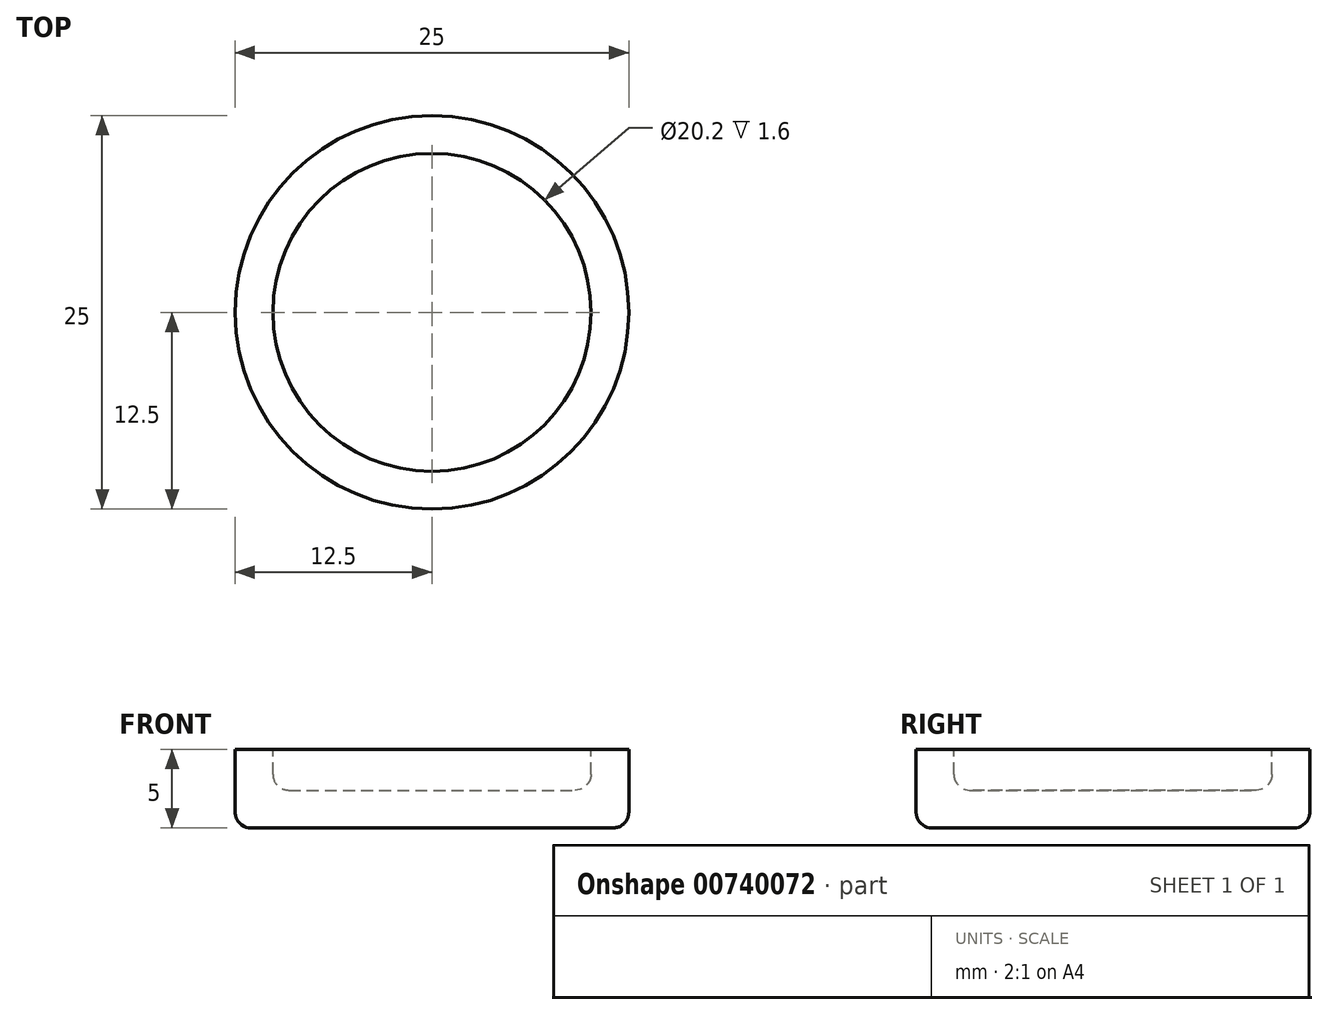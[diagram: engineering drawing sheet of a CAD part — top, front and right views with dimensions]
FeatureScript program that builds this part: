
annotation { "Feature Type Name" : "Feature", "Feature Type Description" : "" }
export const myFeature = defineFeature(function(context is Context, id is Id, definition is map)
    precondition{}
    {
        {
            var Q0;
            Q0=qCreatedBy(makeId("Front.planeOp"),FACE);
            var sketch = newSketch(context, id + "F0", { "sketchPlane" : qUnion([Q0])});
            skLineSegment(sketch, "E0", {"start": v(0, 0) * mm, "end": v(12.5, 0) * mm});
            skLineSegment(sketch, "E1", {"start": v(12.5, 0) * mm, "end": v(12.5, 5) * mm});
            skLineSegment(sketch, "E2", {"start": v(12.5, 5) * mm, "end": v(10.1, 5) * mm});
            skLineSegment(sketch, "E3", {"start": v(10.1, 5) * mm, "end": v(10.1, 2.4) * mm});
            skLineSegment(sketch, "E4", {"start": v(10.1, 2.4) * mm, "end": v(0, 2.4) * mm});
            skLineSegment(sketch, "E5", {"start": v(0, 2.4) * mm, "end": v(0, 0) * mm});
            skSolve(sketch);
        }
        {
            var Q0;
            Q0=makeQuery(id+"F0.imprint","IMPRINT",FACE,{"disambiguationData":[TD([[makeQuery(id+"F0.imprint","IMPRINT",EDGE,{"derivedFrom":sQuery(id+"F0.wireOp",EDGE,"E0")}),1.0]])]});
            var Q1;
            Q1=sQuery(id+"F0.wireOp",EDGE,"E5");
            revolve(context, id + "F1", {"surfaceOperationType" : NewSurfaceOperationType.NEW, "entities" : qUnion([Q0]), "axis" : qUnion([Q1]), "revolveType" : RevolveType.FULL});
        }
        {
            var Q0;
            Q0=makeQuery(id+"F1.opRevolve","SWEPT_EDGE",EDGE,{"disambiguationData":[OSD([sQuery(id+"F0.wireOp",EDGE,"E3"),sQuery(id+"F0.wireOp",EDGE,"E4")])]});
            var Q1;
            Q1=makeQuery(id+"F1.opRevolve","SWEPT_EDGE",EDGE,{"disambiguationData":[OSD([sQuery(id+"F0.wireOp",EDGE,"E0"),sQuery(id+"F0.wireOp",EDGE,"E1")])]});
            fillet(context, id + "F2", {"entities" : qUnion([Q0, Q1]), "radius" : 1 * mm, "tangentPropagation" : true, "allowEdgeOverflow" : false});
        }
    });
